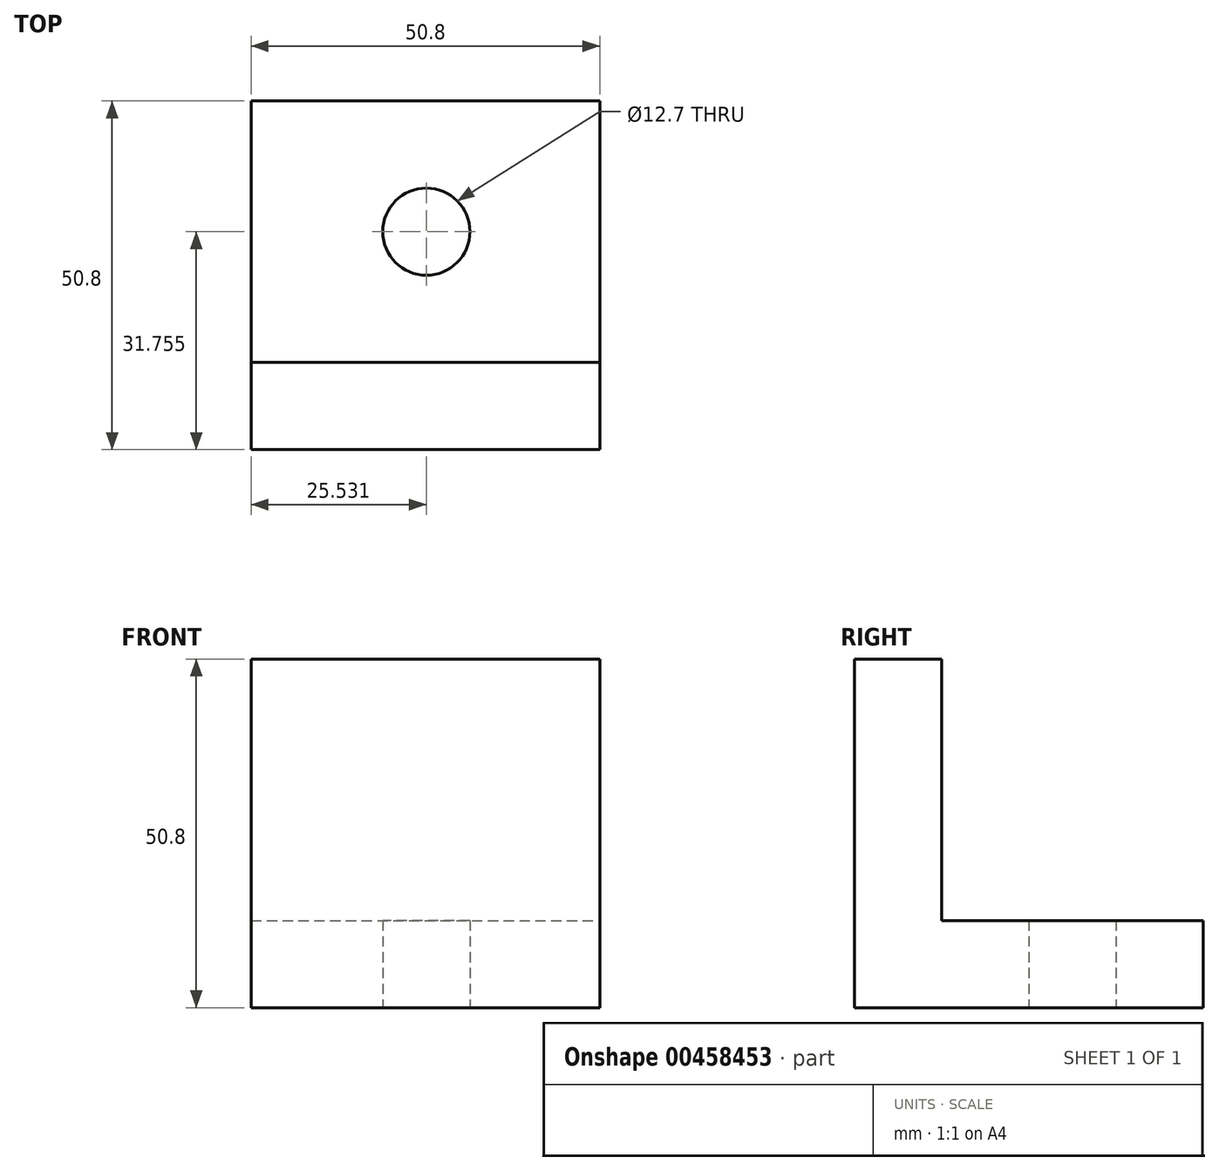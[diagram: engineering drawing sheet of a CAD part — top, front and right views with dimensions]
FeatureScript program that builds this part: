
annotation { "Feature Type Name" : "Feature", "Feature Type Description" : "" }
export const myFeature = defineFeature(function(context is Context, id is Id, definition is map)
    precondition{}
    {
        {
            var Q0;
            Q0=qCreatedBy(makeId("Top.planeOp"),FACE);
            var sketch = newSketch(context, id + "F0", { "sketchPlane" : qUnion([Q0])});
            skLineSegment(sketch, "E0.bottom", {"start": v(-25.02, 50.81) * mm, "end": v(25.78, 50.81) * mm});
            skLineSegment(sketch, "E0.top", {"start": v(-25.02, 0.01) * mm, "end": v(25.78, 0.01) * mm});
            skLineSegment(sketch, "E0.left", {"start": v(-25.02, 50.81) * mm, "end": v(-25.02, 0.01) * mm});
            skLineSegment(sketch, "E0.right", {"start": v(25.78, 50.81) * mm, "end": v(25.78, 0.01) * mm});
            skCircle(sketch, "E1", {"center": v(0.51, 31.76) * mm, "radius": 6.35 * mm});
            skSolve(sketch);
        }
        {
            var Q0;
            Q0=makeQuery(id+"F0.imprint","IMPRINT",FACE,{"disambiguationData":[TD([[makeQuery(id+"F0.imprint","IMPRINT",EDGE,{"derivedFrom":sQuery(id+"F0.wireOp",EDGE,"E0.bottom")}),-1.0]])]});
            extrude(context, id + "F1", {"entities" : qUnion([Q0]), "depth" : 12.7 * mm});
        }
        {
            var Q0;
            Q0=makeQuery(id+"F1.opExtrude","CAP_FACE",FACE,{"disambiguationData":[OSD([sQuery(id+"F0.wireOp",EDGE,"E0.bottom"),sQuery(id+"F0.wireOp",EDGE,"E0.top"),sQuery(id+"F0.wireOp",EDGE,"E0.left"),sQuery(id+"F0.wireOp",EDGE,"E0.right"),sQuery(id+"F0.wireOp",EDGE,"E1")])],"isStart":false});
            var sketch = newSketch(context, id + "F2", { "sketchPlane" : qUnion([Q0])});
            skLineSegment(sketch, "E2.bottom", {"start": v(-25.02, 0.01) * mm, "end": v(25.78, 0.01) * mm});
            skLineSegment(sketch, "E2.top", {"start": v(-25.02, 12.71) * mm, "end": v(25.78, 12.71) * mm});
            skLineSegment(sketch, "E2.left", {"start": v(-25.02, 0.01) * mm, "end": v(-25.02, 12.71) * mm});
            skLineSegment(sketch, "E2.right", {"start": v(25.78, 0.01) * mm, "end": v(25.78, 12.71) * mm});
            skSolve(sketch);
        }
        {
            var Q0;
            Q0=makeQuery(id+"F2.imprint","IMPRINT",FACE,{"disambiguationData":[TD([[makeQuery(id+"F2.imprint","IMPRINT",EDGE,{"derivedFrom":sQuery(id+"F2.wireOp",EDGE,"E2.bottom")}),1.0]])]});
            extrude(context, id + "F3", {"entities" : qUnion([Q0]), "operationType" : NewBodyOperationType.ADD, "depth" : 38.1 * mm});
        }
    });
